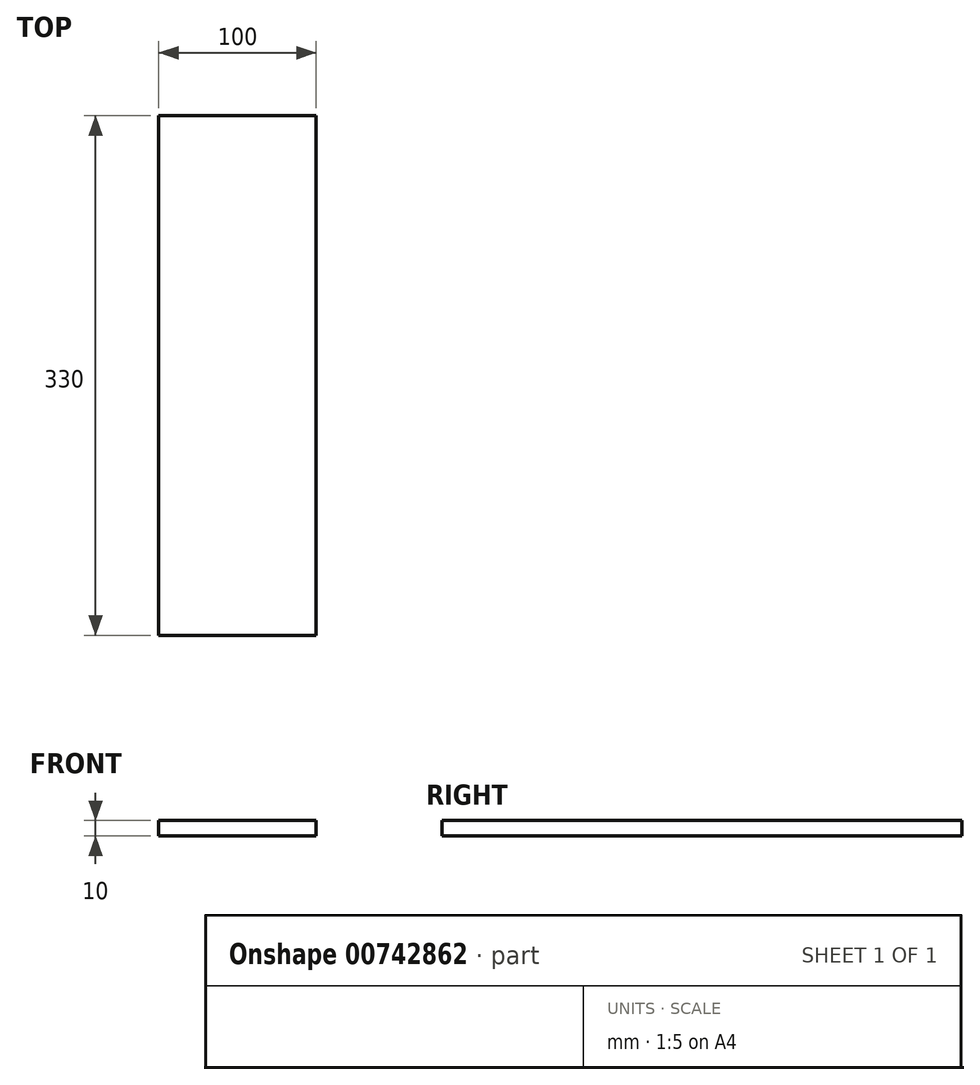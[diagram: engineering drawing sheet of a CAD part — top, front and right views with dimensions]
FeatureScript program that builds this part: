
annotation { "Feature Type Name" : "Feature", "Feature Type Description" : "" }
export const myFeature = defineFeature(function(context is Context, id is Id, definition is map)
    precondition{}
    {
        {
            var Q0;
            Q0=qCreatedBy(makeId("Top.planeOp"),FACE);
            var sketch = newSketch(context, id + "F0", { "sketchPlane" : qUnion([Q0])});
            skLineSegment(sketch, "E0.bottom", {"start": v(50, 165) * mm, "end": v(-50, 165) * mm});
            skLineSegment(sketch, "E0.top", {"start": v(50, -165) * mm, "end": v(-50, -165) * mm});
            skLineSegment(sketch, "E0.left", {"start": v(50, 165) * mm, "end": v(50, -165) * mm});
            skLineSegment(sketch, "E0.right", {"start": v(-50, 165) * mm, "end": v(-50, -165) * mm});
            skPoint(sketch, "E0.middle", {"position": v(0, 0) * mm});
            skSolve(sketch);
        }
        {
            var Q0;
            Q0 = qSketchRegion(id + "F0", true);
            extrude(context, id + "F1", {"entities" : qUnion([Q0]), "endBound" : BoundingType.SYMMETRIC, "depth" : 10 * mm, "offsetDistance" : 25.4 * mm});
        }
    });
